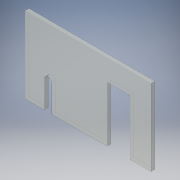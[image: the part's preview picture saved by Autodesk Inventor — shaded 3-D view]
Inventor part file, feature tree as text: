
AUTODESK INVENTOR PART (.ipt)
format: ipt  version: 2016 (Build 200138000, 138)  size: 121,344 bytes
history: native  units: in
note: dims shown in document units (in); Inventor stores cm internally (conversion verified against a paired STEP export)
features: fillet x2, extrude x1, sketch x1
ambient origin geometry x8: Origin, YZ Plane, XZ Plane, XY Plane, X Axis, Y Axis, Z Axis, Center Point
bodies: Solid1 (feature_tree)
feature tree (4):
  extrude  "Extrusion1"  Depth=10.0in
  fillet  "Fillet1"  Radius=3.0in
  fillet  "Fillet2"  Radius=7.25in
  sketch  "Sketch1"  dims[d0=16.5in d1=10.0in d2=3.0in d3=7.25in d4=10.75in d5=1.0in d6=3.5in d7=2.5in d8=1.0in d9=3.0in d10=0.5in d11=0.0in d12=0.125in d13=0.125in]
